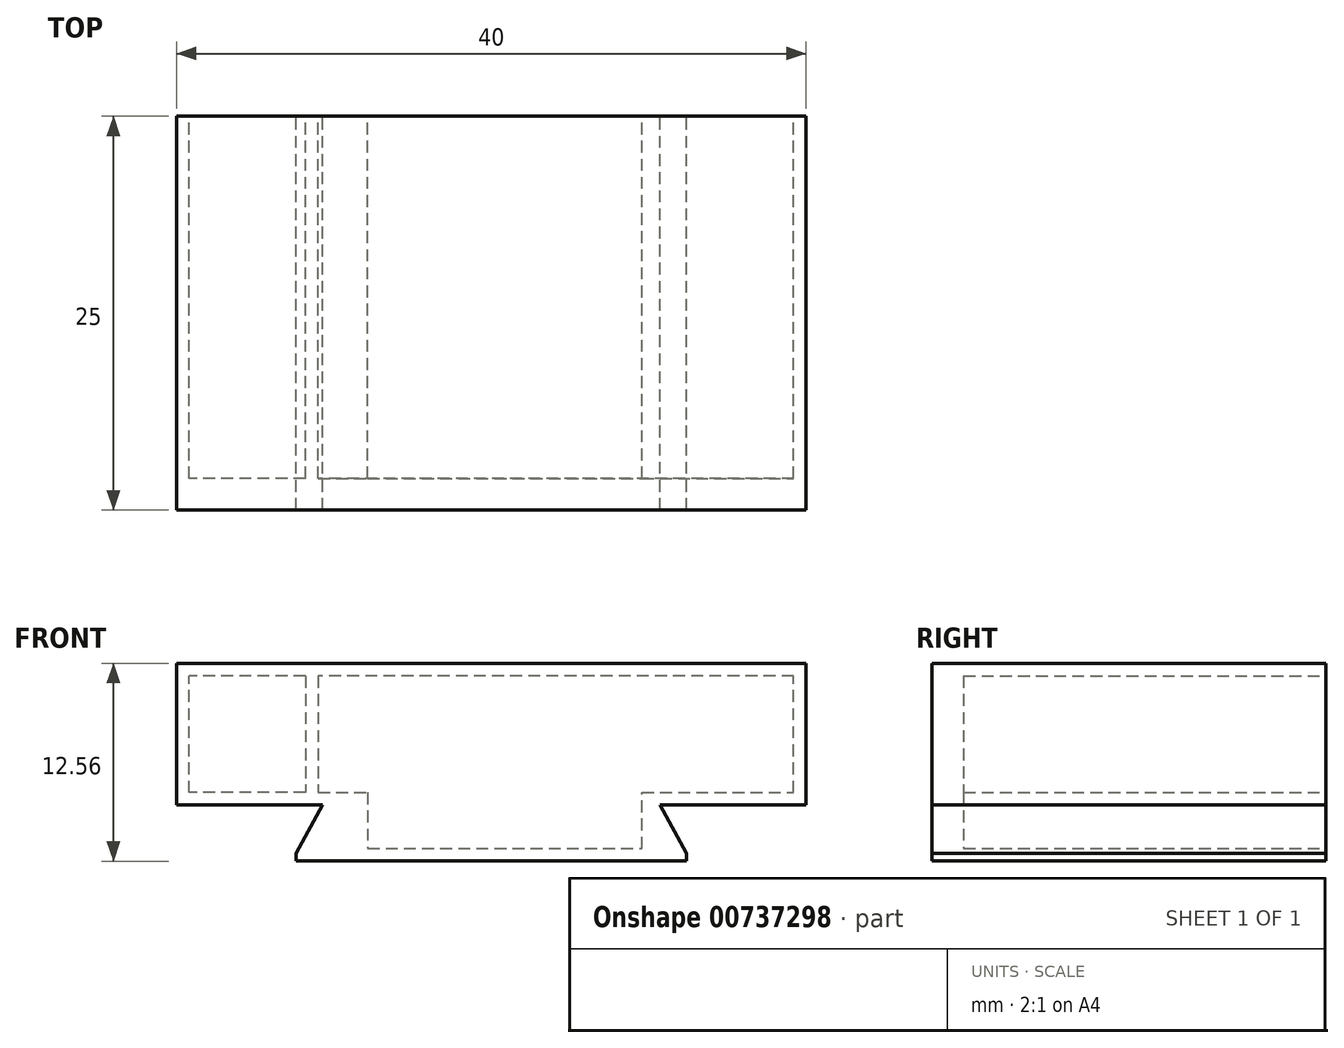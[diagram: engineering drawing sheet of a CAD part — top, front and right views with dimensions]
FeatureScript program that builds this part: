
annotation { "Feature Type Name" : "Feature", "Feature Type Description" : "" }
export const myFeature = defineFeature(function(context is Context, id is Id, definition is map)
    precondition{}
    {
        {
            var Q0;
            Q0=qCreatedBy(makeId("Front.planeOp"),FACE);
            var sketch = newSketch(context, id + "F0", { "sketchPlane" : qUnion([Q0])});
            skLineSegment(sketch, "E0", {"start": v(10.09, -11.19) * mm, "end": v(8.41, -8.13) * mm});
            skLineSegment(sketch, "E1", {"start": v(8.41, -8.13) * mm, "end": v(17.69, -8.13) * mm});
            skLineSegment(sketch, "E2", {"start": v(17.69, -8.13) * mm, "end": v(17.69, 0.87) * mm});
            skLineSegment(sketch, "E3", {"start": v(17.69, 0.87) * mm, "end": v(-22.31, 0.87) * mm});
            skLineSegment(sketch, "E4", {"start": v(-22.31, 0.87) * mm, "end": v(-22.31, -8.13) * mm});
            skLineSegment(sketch, "E5", {"start": v(-22.31, -8.13) * mm, "end": v(-13.04, -8.13) * mm});
            skLineSegment(sketch, "E6", {"start": v(-13.04, -8.13) * mm, "end": v(-14.71, -11.19) * mm});
            skLineSegment(sketch, "E7", {"start": v(10.09, -11.19) * mm, "end": v(10.09, -11.69) * mm});
            skLineSegment(sketch, "E8", {"start": v(10.09, -11.69) * mm, "end": v(-14.71, -11.69) * mm});
            skLineSegment(sketch, "E9", {"start": v(-14.71, -11.69) * mm, "end": v(-14.71, -11.19) * mm});
            skSolve(sketch);
        }
        {
            var Q0;
            Q0 = qSketchRegion(id + "F0", true);
            extrude(context, id + "F1", {"entities" : qUnion([Q0]), "depth" : 25 * mm, "offsetDistance" : 25 * mm});
        }
        {
            var Q0;
            Q0=makeQuery(id+"F1.opExtrude","CAP_FACE",FACE,{"disambiguationData":[OSD([sQuery(id+"F0.wireOp",EDGE,"E0"),sQuery(id+"F0.wireOp",EDGE,"E1"),sQuery(id+"F0.wireOp",EDGE,"E2"),sQuery(id+"F0.wireOp",EDGE,"E3"),sQuery(id+"F0.wireOp",EDGE,"E4"),sQuery(id+"F0.wireOp",EDGE,"E5"),sQuery(id+"F0.wireOp",EDGE,"E6"),sQuery(id+"F0.wireOp",EDGE,"E7"),sQuery(id+"F0.wireOp",EDGE,"E8"),sQuery(id+"F0.wireOp",EDGE,"E9")])],"isStart":true});
            var sketch = newSketch(context, id + "F2", { "sketchPlane" : qUnion([Q0])});
            skLineSegment(sketch, "E10", {"start": v(-7.26, -10.89) * mm, "end": v(-7.26, -7.33) * mm});
            skLineSegment(sketch, "E11", {"start": v(-7.26, -7.33) * mm, "end": v(-16.89, -7.33) * mm});
            skLineSegment(sketch, "E12", {"start": v(-16.89, -7.33) * mm, "end": v(-16.89, 0.07) * mm});
            skLineSegment(sketch, "E13", {"start": v(14.11, 0.07) * mm, "end": v(14.11, -7.33) * mm});
            skLineSegment(sketch, "E14", {"start": v(10.16, -7.33) * mm, "end": v(10.16, -10.89) * mm});
            skLineSegment(sketch, "E15", {"start": v(10.16, -10.89) * mm, "end": v(-7.26, -10.89) * mm});
            skLineSegment(sketch, "E16", {"start": v(13.31, 0.07) * mm, "end": v(13.31, -7.33) * mm});
            skLineSegment(sketch, "E17", {"start": v(21.51, -7.33) * mm, "end": v(21.51, 0.07) * mm});
            skLineSegment(sketch, "E18", {"start": v(14.11, -7.33) * mm, "end": v(21.51, -7.33) * mm});
            skLineSegment(sketch, "E19", {"start": v(13.31, -7.33) * mm, "end": v(10.16, -7.33) * mm});
            skLineSegment(sketch, "E20", {"start": v(-16.89, 0.07) * mm, "end": v(13.31, 0.07) * mm});
            skLineSegment(sketch, "E21", {"start": v(14.11, 0.07) * mm, "end": v(21.51, 0.07) * mm});
            skSolve(sketch);
        }
        {
            var Q0;
            Q0 = qSketchRegion(id + "F2", true);
            extrude(context, id + "F3", {"entities" : qUnion([Q0]), "operationType" : NewBodyOperationType.REMOVE, "oppositeDirection" : true, "depth" : 23 * mm, "offsetDistance" : 25 * mm});
        }
    });
